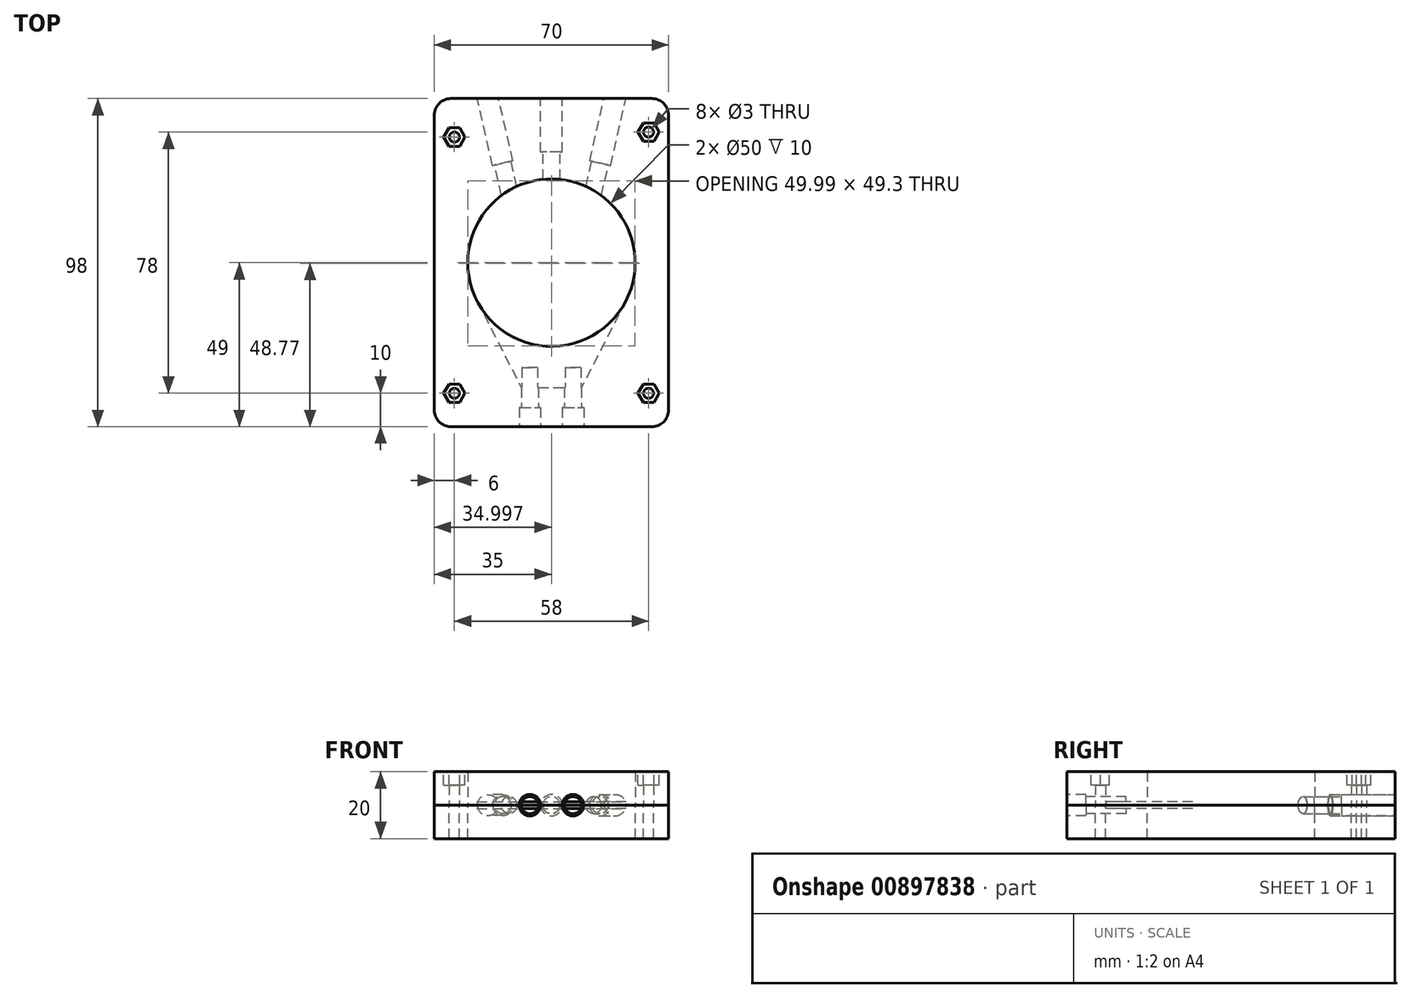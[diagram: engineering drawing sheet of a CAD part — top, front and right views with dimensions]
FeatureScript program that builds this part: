
annotation { "Feature Type Name" : "Feature", "Feature Type Description" : "" }
export const myFeature = defineFeature(function(context is Context, id is Id, definition is map)
    precondition{}
    {
        {
            var Q0;
            Q0=qCreatedBy(makeId("Front.planeOp"),FACE);
            var sketch = newSketch(context, id + "F0", { "sketchPlane" : qUnion([Q0])});
            skLineSegment(sketch, "E0.bottom", {"start": v(35, 5) * mm, "end": v(-35, 5) * mm});
            skLineSegment(sketch, "E0.top", {"start": v(35, -5) * mm, "end": v(-35, -5) * mm});
            skLineSegment(sketch, "E0.left", {"start": v(35, 5) * mm, "end": v(35, -5) * mm});
            skLineSegment(sketch, "E0.right", {"start": v(-35, 5) * mm, "end": v(-35, -5) * mm});
            skPoint(sketch, "E0.middle", {"position": v(0, 0) * mm});
            skSolve(sketch);
        }
        {
            var Q0;
            Q0 = qSketchRegion(id + "F0", true);
            extrude(context, id + "F1", {"entities" : qUnion([Q0]), "endBound" : BoundingType.SYMMETRIC, "depth" : 98 * mm, "offsetDistance" : 25 * mm});
        }
        {
            var Q0;
            Q0=makeQuery(id+"F1.opExtrude","SWEPT_FACE",FACE,{"disambiguationData":[OSD([sQuery(id+"F0.wireOp",EDGE,"E0.bottom")])]});
            var sketch = newSketch(context, id + "F2", { "sketchPlane" : qUnion([Q0])});
            skCircle(sketch, "E1", {"center": v(0, 0) * mm, "radius": 25 * mm});
            skSolve(sketch);
        }
        {
            var Q0;
            Q0 = qSketchRegion(id + "F2", true);
            extrude(context, id + "F3", {"entities" : qUnion([Q0]), "operationType" : NewBodyOperationType.REMOVE, "endBound" : BoundingType.THROUGH_ALL, "oppositeDirection" : true, "depth" : 25 * mm, "offsetDistance" : 25 * mm});
        }
        {
            var Q0;
            Q0=makeQuery(id+"F1.opExtrude","CAP_FACE",FACE,{"disambiguationData":[OSD([sQuery(id+"F0.wireOp",EDGE,"E0.bottom"),sQuery(id+"F0.wireOp",EDGE,"E0.top"),sQuery(id+"F0.wireOp",EDGE,"E0.left"),sQuery(id+"F0.wireOp",EDGE,"E0.right")])],"isStart":false});
            var sketch = newSketch(context, id + "F4", { "sketchPlane" : qUnion([Q0])});
            skCircle(sketch, "E2", {"center": v(-6.44, 5) * mm, "radius": 3.2 * mm});
            skCircle(sketch, "E3", {"center": v(6.44, 5) * mm, "radius": 3.2 * mm});
            skSolve(sketch);
        }
        {
            var Q0;
            Q0 = qSketchRegion(id + "F4", true);
            extrude(context, id + "F5", {"entities" : qUnion([Q0]), "operationType" : NewBodyOperationType.REMOVE, "oppositeDirection" : true, "depth" : 5.68 * mm, "offsetDistance" : 25 * mm});
        }
        {
            var Q0;
            Q0=makeQuery(id+"F5.boolean.opBoolean","COPY",FACE,{"derivedFrom":makeQuery(id+"F5.opExtrude","CAP_FACE",FACE,{"disambiguationData":[OSD([sQuery(id+"F4.wireOp",EDGE,"E2")])],"isStart":false})});
            var sketch = newSketch(context, id + "F6", { "sketchPlane" : qUnion([Q0])});
            skCircle(sketch, "E4", {"center": v(-6.44, 5) * mm, "radius": 2.55 * mm});
            skCircle(sketch, "E5", {"center": v(6.44, 5) * mm, "radius": 2.55 * mm});
            skSolve(sketch);
        }
        {
            var Q0;
            Q0 = qSketchRegion(id + "F6", true);
            extrude(context, id + "F7", {"entities" : qUnion([Q0]), "operationType" : NewBodyOperationType.REMOVE, "oppositeDirection" : true, "depth" : 12 * mm, "offsetDistance" : 25 * mm});
        }
        {
            var Q0;
            Q0=makeQuery(id+"F1.opExtrude","SWEPT_FACE",FACE,{"disambiguationData":[OSD([sQuery(id+"F0.wireOp",EDGE,"E0.bottom")])]});
            var sketch = newSketch(context, id + "F8", { "sketchPlane" : qUnion([Q0])});
            skLineSegment(sketch, "E6", {"start": v(-22.26, -11.39) * mm, "end": v(-9, -37.32) * mm});
            skLineSegment(sketch, "E7", {"start": v(0, 0) * mm, "end": v(0, -57.89) * mm, "construction": true});
            skLineSegment(sketch, "E8.MirrorCS", {"start": v(22.26, -11.39) * mm, "end": v(9, -37.32) * mm});
            skLineSegment(sketch, "E9", {"start": v(-9, -37.32) * mm, "end": v(9, -37.32) * mm});
            skLineSegment(sketch, "E10", {"start": v(22.26, -11.39) * mm, "end": v(-22.26, -11.39) * mm});
            skSolve(sketch);
        }
        {
            var Q0;
            Q0 = qSketchRegion(id + "F8", true);
            extrude(context, id + "F9", {"entities" : qUnion([Q0]), "operationType" : NewBodyOperationType.REMOVE, "oppositeDirection" : true, "depth" : 1 * mm, "offsetDistance" : 25 * mm});
        }
        {
            var Q0;
            Q0=makeQuery(id+"F1.opExtrude","CAP_FACE",FACE,{"disambiguationData":[OSD([sQuery(id+"F0.wireOp",EDGE,"E0.bottom"),sQuery(id+"F0.wireOp",EDGE,"E0.top"),sQuery(id+"F0.wireOp",EDGE,"E0.left"),sQuery(id+"F0.wireOp",EDGE,"E0.right")])],"isStart":true});
            var Q1;
            Q1=makeQuery(id+"F1.opExtrude","CAP_EDGE",EDGE,{"disambiguationData":[OSD([sQuery(id+"F0.wireOp",EDGE,"E0.right")])],"isStart":true});
            cPlane(context, id + "F10", {"entities" : qUnion([Q0, Q1]), "cplaneType" : CPlaneType.LINE_ANGLE, "offset" : 25 * mm, "angle" : 13 * degree, "oppositeDirection" : true, "width" : 150 * mm, "height" : 150 * mm});
        }
        {
            var Q0;
            Q0=makeQuery(id+"F1.opExtrude","CAP_FACE",FACE,{"disambiguationData":[OSD([sQuery(id+"F0.wireOp",EDGE,"E0.bottom"),sQuery(id+"F0.wireOp",EDGE,"E0.top"),sQuery(id+"F0.wireOp",EDGE,"E0.left"),sQuery(id+"F0.wireOp",EDGE,"E0.right")])],"isStart":true});
            var Q1;
            Q1=makeQuery(id+"F1.opExtrude","CAP_EDGE",EDGE,{"disambiguationData":[OSD([sQuery(id+"F0.wireOp",EDGE,"E0.left")])],"isStart":true});
            cPlane(context, id + "F11", {"entities" : qUnion([Q0, Q1]), "cplaneType" : CPlaneType.LINE_ANGLE, "offset" : 25 * mm, "angle" : 13 * degree, "width" : 150 * mm, "height" : 150 * mm});
        }
        {
            var Q0;
            Q0=qCreatedBy(id+"F10.planeOp",FACE);
            var sketch = newSketch(context, id + "F12", { "sketchPlane" : qUnion([Q0])});
            skCircle(sketch, "E11", {"center": v(-7.48, 5) * mm, "radius": 3.1 * mm});
            skSolve(sketch);
        }
        {
            var Q0;
            Q0 = qSketchRegion(id + "F12", true);
            extrude(context, id + "F13", {"entities" : qUnion([Q0]), "operationType" : NewBodyOperationType.REMOVE, "depth" : 15 * mm, "offsetDistance" : 25 * mm});
        }
        {
            var Q0;
            Q0=qCreatedBy(id+"F11.planeOp",FACE);
            var sketch = newSketch(context, id + "F14", { "sketchPlane" : qUnion([Q0])});
            skCircle(sketch, "E12", {"center": v(7.48, 5) * mm, "radius": 3.2 * mm});
            skSolve(sketch);
        }
        {
            var Q0;
            Q0 = qSketchRegion(id + "F14", true);
            extrude(context, id + "F15", {"entities" : qUnion([Q0]), "operationType" : NewBodyOperationType.REMOVE, "depth" : 23.4 * mm, "offsetDistance" : 25 * mm});
        }
        {
            var Q0;
            Q0 = qSketchRegion(id + "F12", true);
            extrude(context, id + "F16", {"entities" : qUnion([Q0]), "operationType" : NewBodyOperationType.REMOVE, "depth" : 23.4 * mm, "offsetDistance" : 25 * mm});
        }
        {
            var Q0;
            Q0=makeQuery(id+"F16.boolean.opBoolean","COPY",FACE,{"derivedFrom":makeQuery(id+"F16.opExtrude","CAP_FACE",FACE,{"disambiguationData":[OSD([sQuery(id+"F12.wireOp",EDGE,"E11")])],"isStart":false})});
            var sketch = newSketch(context, id + "F17", { "sketchPlane" : qUnion([Q0])});
            skCircle(sketch, "E13", {"center": v(7.48, 5) * mm, "radius": 2.55 * mm});
            skSolve(sketch);
        }
        {
            var Q0;
            Q0 = qSketchRegion(id + "F17", true);
            extrude(context, id + "F18", {"entities" : qUnion([Q0]), "operationType" : NewBodyOperationType.REMOVE, "oppositeDirection" : true, "depth" : 25 * mm, "offsetDistance" : 25 * mm});
        }
        {
            var Q0;
            Q0=makeQuery(id+"F15.boolean.opBoolean","COPY",FACE,{"derivedFrom":makeQuery(id+"F15.opExtrude","CAP_FACE",FACE,{"disambiguationData":[OSD([sQuery(id+"F14.wireOp",EDGE,"E12")])],"isStart":false})});
            var sketch = newSketch(context, id + "F19", { "sketchPlane" : qUnion([Q0])});
            skCircle(sketch, "E14", {"center": v(-7.48, 5) * mm, "radius": 2.55 * mm});
            skSolve(sketch);
        }
        {
            var Q0;
            Q0 = qSketchRegion(id + "F19", true);
            extrude(context, id + "F20", {"entities" : qUnion([Q0]), "operationType" : NewBodyOperationType.REMOVE, "oppositeDirection" : true, "depth" : 25 * mm, "offsetDistance" : 25 * mm});
        }
        {
            var Q0;
            Q0=makeQuery(id+"F1.opExtrude","CAP_FACE",FACE,{"disambiguationData":[OSD([sQuery(id+"F0.wireOp",EDGE,"E0.bottom"),sQuery(id+"F0.wireOp",EDGE,"E0.top"),sQuery(id+"F0.wireOp",EDGE,"E0.left"),sQuery(id+"F0.wireOp",EDGE,"E0.right")])],"isStart":true});
            var sketch = newSketch(context, id + "F21", { "sketchPlane" : qUnion([Q0])});
            skCircle(sketch, "E15", {"center": v(0, 5) * mm, "radius": 2.55 * mm});
            skSolve(sketch);
        }
        {
            var Q0;
            Q0 = qSketchRegion(id + "F21", true);
            extrude(context, id + "F22", {"entities" : qUnion([Q0]), "operationType" : NewBodyOperationType.REMOVE, "oppositeDirection" : true, "depth" : 25 * mm, "offsetDistance" : 25 * mm});
        }
        {
            var Q0;
            Q0=makeQuery(id+"F1.opExtrude","CAP_FACE",FACE,{"disambiguationData":[OSD([sQuery(id+"F0.wireOp",EDGE,"E0.bottom"),sQuery(id+"F0.wireOp",EDGE,"E0.top"),sQuery(id+"F0.wireOp",EDGE,"E0.left"),sQuery(id+"F0.wireOp",EDGE,"E0.right")])],"isStart":true});
            var sketch = newSketch(context, id + "F23", { "sketchPlane" : qUnion([Q0])});
            skCircle(sketch, "E16", {"center": v(0, 5) * mm, "radius": 3.2 * mm});
            skSolve(sketch);
        }
        {
            var Q0;
            Q0 = qSketchRegion(id + "F23", true);
            extrude(context, id + "F24", {"entities" : qUnion([Q0]), "operationType" : NewBodyOperationType.REMOVE, "oppositeDirection" : true, "depth" : 16 * mm, "offsetDistance" : 25 * mm});
        }
        {
            var Q0;
            {var subQ0=sQuery(id+"F0.wireOp",EDGE,"E0.bottom");var subQ1=makeQuery(id+"F1.opExtrude","SWEPT_FACE",FACE,{"disambiguationData":[OSD([subQ0])]});var subQ2=sQuery(id+"F8.wireOp",EDGE,"E6");var subQ3=makeQuery(id+"F9.opExtrude","SWEPT_FACE",FACE,{"disambiguationData":[OSD([subQ2])]});var subQ4=makeQuery(id+"F7.boolean.opBoolean","COPY",FACE,{"derivedFrom":makeQuery(id+"F7.opExtrude","SWEPT_FACE",FACE,{"disambiguationData":[OSD([sQuery(id+"F6.wireOp",EDGE,"E4")])]})});var subQ5=sQuery(id+"F8.wireOp",EDGE,"E9");var subQ6=sQuery(id+"F8.wireOp",EDGE,"E8.MirrorCS");var subQ7=makeQuery(id+"F9.opExtrude","SWEPT_FACE",FACE,{"disambiguationData":[OSD([subQ5])]});var subQ9=sQuery(id+"F4.wireOp",EDGE,"E2");var subQ10=makeQuery(id+"F5.boolean.opBoolean","COPY",FACE,{"derivedFrom":makeQuery(id+"F5.opExtrude","CAP_FACE",FACE,{"disambiguationData":[OSD([subQ9])],"isStart":false})});var subQ11=makeQuery(id+"F5.boolean.opBoolean","COPY",FACE,{"derivedFrom":makeQuery(id+"F5.opExtrude","SWEPT_FACE",FACE,{"disambiguationData":[OSD([subQ9])]})});var subQ12=sQuery(id+"F0.wireOp",EDGE,"E0.right");var subQ13=sQuery(id+"F0.wireOp",EDGE,"E0.left");var subQ14=sQuery(id+"F0.wireOp",EDGE,"E0.top");var subQ15=makeQuery(id+"F1.opExtrude","CAP_FACE",FACE,{"disambiguationData":[OSD([subQ0,subQ14,subQ13,subQ12])],"isStart":true});var subQ16=makeQuery(id+"F1.opExtrude","CAP_FACE",FACE,{"disambiguationData":[OSD([subQ0,subQ14,subQ13,subQ12])],"isStart":false});var subQ17=makeQuery(id+"F1.opExtrude","SWEPT_FACE",FACE,{"disambiguationData":[OSD([subQ12])]});var subQ18=makeQuery(id+"F3.boolean.opBoolean","COPY",FACE,{"derivedFrom":makeQuery(id+"F3.opExtrude","SWEPT_FACE",FACE,{"disambiguationData":[OSD([sQuery(id+"F2.wireOp",EDGE,"E1")])]})});var subQ19=sQuery(id+"F4.wireOp",EDGE,"E3");Q0=makeQuery(id+"F18.boolean.opBoolean","SPLIT",FACE,{"disambiguationData":[TD([subQ17])],"derivedFrom":makeQuery(id+"F9.boolean.opBoolean","SPLIT",FACE,{"disambiguationData":[TD([subQ15,subQ16,makeQuery(id+"F1.opExtrude","SWEPT_FACE",FACE,{"disambiguationData":[OSD([subQ13])]}),subQ17,subQ18,subQ11,subQ10,makeQuery(id+"F5.boolean.opBoolean","COPY",FACE,{"derivedFrom":makeQuery(id+"F5.opExtrude","SWEPT_FACE",FACE,{"disambiguationData":[OSD([subQ19])]})}),makeQuery(id+"F5.boolean.opBoolean","COPY",FACE,{"derivedFrom":makeQuery(id+"F5.opExtrude","CAP_FACE",FACE,{"disambiguationData":[OSD([subQ19])],"isStart":false})}),subQ4,makeQuery(id+"F7.boolean.opBoolean","COPY",FACE,{"derivedFrom":makeQuery(id+"F7.opExtrude","SWEPT_FACE",FACE,{"disambiguationData":[OSD([sQuery(id+"F6.wireOp",EDGE,"E5")])]})}),subQ3,makeQuery(id+"F9.opExtrude","SWEPT_FACE",FACE,{"disambiguationData":[OSD([subQ6])]}),subQ7])],"derivedFrom":subQ1})});}
            var sketch = newSketch(context, id + "F25", { "sketchPlane" : qUnion([Q0])});
            skCircle(sketch, "E17", {"center": v(-29, 37.5) * mm, "radius": 1.5 * mm});
            skCircle(sketch, "E18", {"center": v(29, 39) * mm, "radius": 1.5 * mm});
            skCircle(sketch, "E19", {"center": v(-29, -39) * mm, "radius": 1.5 * mm});
            skCircle(sketch, "E20", {"center": v(29, -39) * mm, "radius": 1.5 * mm});
            skSolve(sketch);
        }
        {
            var Q0;
            Q0 = qSketchRegion(id + "F25", true);
            extrude(context, id + "F26", {"entities" : qUnion([Q0]), "operationType" : NewBodyOperationType.REMOVE, "oppositeDirection" : true, "depth" : 25 * mm, "offsetDistance" : 25 * mm});
        }
        {
            var Q0;
            Q0=makeQuery(id+"F1.opExtrude","SWEPT_BODY",BODY,{"disambiguationData":[OSD([sQuery(id+"F0.wireOp",EDGE,"E0.bottom"),sQuery(id+"F0.wireOp",EDGE,"E0.top"),sQuery(id+"F0.wireOp",EDGE,"E0.left"),sQuery(id+"F0.wireOp",EDGE,"E0.right")])]});
            var Q1;
            {var subQ0=sQuery(id+"F0.wireOp",EDGE,"E0.bottom");var subQ1=makeQuery(id+"F1.opExtrude","SWEPT_FACE",FACE,{"disambiguationData":[OSD([subQ0])]});var subQ2=sQuery(id+"F8.wireOp",EDGE,"E6");var subQ3=makeQuery(id+"F9.opExtrude","SWEPT_FACE",FACE,{"disambiguationData":[OSD([subQ2])]});var subQ4=makeQuery(id+"F7.boolean.opBoolean","COPY",FACE,{"derivedFrom":makeQuery(id+"F7.opExtrude","SWEPT_FACE",FACE,{"disambiguationData":[OSD([sQuery(id+"F6.wireOp",EDGE,"E4")])]})});var subQ5=sQuery(id+"F8.wireOp",EDGE,"E9");var subQ6=sQuery(id+"F8.wireOp",EDGE,"E8.MirrorCS");var subQ7=makeQuery(id+"F9.opExtrude","SWEPT_FACE",FACE,{"disambiguationData":[OSD([subQ5])]});var subQ9=sQuery(id+"F4.wireOp",EDGE,"E2");var subQ10=makeQuery(id+"F5.boolean.opBoolean","COPY",FACE,{"derivedFrom":makeQuery(id+"F5.opExtrude","CAP_FACE",FACE,{"disambiguationData":[OSD([subQ9])],"isStart":false})});var subQ11=makeQuery(id+"F5.boolean.opBoolean","COPY",FACE,{"derivedFrom":makeQuery(id+"F5.opExtrude","SWEPT_FACE",FACE,{"disambiguationData":[OSD([subQ9])]})});var subQ12=sQuery(id+"F0.wireOp",EDGE,"E0.right");var subQ13=sQuery(id+"F0.wireOp",EDGE,"E0.left");var subQ14=sQuery(id+"F0.wireOp",EDGE,"E0.top");var subQ15=makeQuery(id+"F1.opExtrude","CAP_FACE",FACE,{"disambiguationData":[OSD([subQ0,subQ14,subQ13,subQ12])],"isStart":true});var subQ16=makeQuery(id+"F1.opExtrude","CAP_FACE",FACE,{"disambiguationData":[OSD([subQ0,subQ14,subQ13,subQ12])],"isStart":false});var subQ17=makeQuery(id+"F1.opExtrude","SWEPT_FACE",FACE,{"disambiguationData":[OSD([subQ12])]});var subQ18=makeQuery(id+"F3.boolean.opBoolean","COPY",FACE,{"derivedFrom":makeQuery(id+"F3.opExtrude","SWEPT_FACE",FACE,{"disambiguationData":[OSD([sQuery(id+"F2.wireOp",EDGE,"E1")])]})});var subQ19=sQuery(id+"F4.wireOp",EDGE,"E3");Q1=makeQuery(id+"F18.boolean.opBoolean","SPLIT",FACE,{"disambiguationData":[TD([subQ17])],"derivedFrom":makeQuery(id+"F9.boolean.opBoolean","SPLIT",FACE,{"disambiguationData":[TD([subQ15,subQ16,makeQuery(id+"F1.opExtrude","SWEPT_FACE",FACE,{"disambiguationData":[OSD([subQ13])]}),subQ17,subQ18,subQ11,subQ10,makeQuery(id+"F5.boolean.opBoolean","COPY",FACE,{"derivedFrom":makeQuery(id+"F5.opExtrude","SWEPT_FACE",FACE,{"disambiguationData":[OSD([subQ19])]})}),makeQuery(id+"F5.boolean.opBoolean","COPY",FACE,{"derivedFrom":makeQuery(id+"F5.opExtrude","CAP_FACE",FACE,{"disambiguationData":[OSD([subQ19])],"isStart":false})}),subQ4,makeQuery(id+"F7.boolean.opBoolean","COPY",FACE,{"derivedFrom":makeQuery(id+"F7.opExtrude","SWEPT_FACE",FACE,{"disambiguationData":[OSD([sQuery(id+"F6.wireOp",EDGE,"E5")])]})}),subQ3,makeQuery(id+"F9.opExtrude","SWEPT_FACE",FACE,{"disambiguationData":[OSD([subQ6])]}),subQ7])],"derivedFrom":subQ1})});}
            mirror(context, id + "F27", {"entities" : qUnion([Q0]), "mirrorPlane" : qUnion([Q1])});
        }
        {
            var Q0;
            Q0=makeQuery(id+"F27.opPattern","COPY",FACE,{"derivedFrom":makeQuery(id+"F1.opExtrude","SWEPT_FACE",FACE,{"disambiguationData":[OSD([sQuery(id+"F0.wireOp",EDGE,"E0.top")])]}),"instanceName":"1"});
            var sketch = newSketch(context, id + "F28", { "sketchPlane" : qUnion([Q0])});
            skCircle(sketch, "E21.cCircle", {"center": v(-29, 37.5) * mm, "radius": 2.75 * mm, "construction": true});
            skLineSegment(sketch, "E21.0", {"start": v(-25.82, 37.5) * mm, "end": v(-27.41, 34.75) * mm});
            skLineSegment(sketch, "E21.1", {"start": v(-27.41, 34.75) * mm, "end": v(-30.59, 34.75) * mm});
            skLineSegment(sketch, "E21.2", {"start": v(-30.59, 34.75) * mm, "end": v(-32.18, 37.5) * mm});
            skLineSegment(sketch, "E21.3", {"start": v(-32.18, 37.5) * mm, "end": v(-30.59, 40.25) * mm});
            skLineSegment(sketch, "E21.4", {"start": v(-30.59, 40.25) * mm, "end": v(-27.41, 40.25) * mm});
            skLineSegment(sketch, "E21.5", {"start": v(-27.41, 40.25) * mm, "end": v(-25.82, 37.5) * mm});
            skPoint(sketch, "E21.0.midPoint", {"position": v(-26.62, 36.13) * mm});
            skCircle(sketch, "E22.cCircle", {"center": v(29, 39) * mm, "radius": 2.75 * mm, "construction": true});
            skLineSegment(sketch, "E22.0", {"start": v(32.18, 39) * mm, "end": v(30.59, 36.25) * mm});
            skLineSegment(sketch, "E22.1", {"start": v(30.59, 36.25) * mm, "end": v(27.41, 36.25) * mm});
            skLineSegment(sketch, "E22.2", {"start": v(27.41, 36.25) * mm, "end": v(25.82, 39) * mm});
            skLineSegment(sketch, "E22.3", {"start": v(25.82, 39) * mm, "end": v(27.41, 41.75) * mm});
            skLineSegment(sketch, "E22.4", {"start": v(27.41, 41.75) * mm, "end": v(30.59, 41.75) * mm});
            skLineSegment(sketch, "E22.5", {"start": v(30.59, 41.75) * mm, "end": v(32.18, 39) * mm});
            skPoint(sketch, "E22.0.midPoint", {"position": v(31.38, 37.62) * mm});
            skCircle(sketch, "E23.cCircle", {"center": v(-29, -39) * mm, "radius": 2.75 * mm, "construction": true});
            skLineSegment(sketch, "E23.0", {"start": v(-25.82, -39) * mm, "end": v(-27.41, -41.75) * mm});
            skLineSegment(sketch, "E23.1", {"start": v(-27.41, -41.75) * mm, "end": v(-30.59, -41.75) * mm});
            skLineSegment(sketch, "E23.2", {"start": v(-30.59, -41.75) * mm, "end": v(-32.18, -39) * mm});
            skLineSegment(sketch, "E23.3", {"start": v(-32.18, -39) * mm, "end": v(-30.59, -36.25) * mm});
            skLineSegment(sketch, "E23.4", {"start": v(-30.59, -36.25) * mm, "end": v(-27.41, -36.25) * mm});
            skLineSegment(sketch, "E23.5", {"start": v(-27.41, -36.25) * mm, "end": v(-25.82, -39) * mm});
            skPoint(sketch, "E23.0.midPoint", {"position": v(-26.62, -40.38) * mm});
            skCircle(sketch, "E24.cCircle", {"center": v(29, -39) * mm, "radius": 2.75 * mm, "construction": true});
            skLineSegment(sketch, "E24.0", {"start": v(30.59, -41.75) * mm, "end": v(27.41, -41.75) * mm});
            skLineSegment(sketch, "E24.1", {"start": v(27.41, -41.75) * mm, "end": v(25.82, -39) * mm});
            skLineSegment(sketch, "E24.2", {"start": v(25.82, -39) * mm, "end": v(27.41, -36.25) * mm});
            skLineSegment(sketch, "E24.3", {"start": v(27.41, -36.25) * mm, "end": v(30.59, -36.25) * mm});
            skLineSegment(sketch, "E24.4", {"start": v(30.59, -36.25) * mm, "end": v(32.18, -39) * mm});
            skLineSegment(sketch, "E24.5", {"start": v(32.18, -39) * mm, "end": v(30.59, -41.75) * mm});
            skPoint(sketch, "E24.0.midPoint", {"position": v(29, -41.75) * mm});
            skSolve(sketch);
        }
        {
            var Q0;
            Q0 = qSketchRegion(id + "F28", true);
            extrude(context, id + "F29", {"entities" : qUnion([Q0]), "operationType" : NewBodyOperationType.REMOVE, "oppositeDirection" : true, "depth" : 4 * mm, "offsetDistance" : 25 * mm});
        }
        {
            var Q0;
            Q0=makeQuery(id+"F27.opPattern","COPY",EDGE,{"derivedFrom":makeQuery(id+"F1.opExtrude","CAP_EDGE",EDGE,{"disambiguationData":[OSD([sQuery(id+"F0.wireOp",EDGE,"E0.right")])],"isStart":false}),"instanceName":"1"});
            var Q1;
            Q1=makeQuery(id+"F1.opExtrude","CAP_EDGE",EDGE,{"disambiguationData":[OSD([sQuery(id+"F0.wireOp",EDGE,"E0.right")])],"isStart":false});
            var Q2;
            Q2=makeQuery(id+"F27.opPattern","COPY",EDGE,{"derivedFrom":makeQuery(id+"F1.opExtrude","CAP_EDGE",EDGE,{"disambiguationData":[OSD([sQuery(id+"F0.wireOp",EDGE,"E0.left")])],"isStart":false}),"instanceName":"1"});
            var Q3;
            Q3=makeQuery(id+"F1.opExtrude","CAP_EDGE",EDGE,{"disambiguationData":[OSD([sQuery(id+"F0.wireOp",EDGE,"E0.left")])],"isStart":false});
            var Q4;
            Q4=makeQuery(id+"F27.opPattern","COPY",EDGE,{"derivedFrom":makeQuery(id+"F1.opExtrude","CAP_EDGE",EDGE,{"disambiguationData":[OSD([sQuery(id+"F0.wireOp",EDGE,"E0.left")])],"isStart":true}),"instanceName":"1"});
            var Q5;
            Q5=makeQuery(id+"F1.opExtrude","CAP_EDGE",EDGE,{"disambiguationData":[OSD([sQuery(id+"F0.wireOp",EDGE,"E0.left")])],"isStart":true});
            var Q6;
            Q6=makeQuery(id+"F27.opPattern","COPY",EDGE,{"derivedFrom":makeQuery(id+"F1.opExtrude","CAP_EDGE",EDGE,{"disambiguationData":[OSD([sQuery(id+"F0.wireOp",EDGE,"E0.right")])],"isStart":true}),"instanceName":"1"});
            var Q7;
            Q7=makeQuery(id+"F1.opExtrude","CAP_EDGE",EDGE,{"disambiguationData":[OSD([sQuery(id+"F0.wireOp",EDGE,"E0.right")])],"isStart":true});
            fillet(context, id + "F30", {"entities" : qUnion([Q0, Q1, Q2, Q3, Q4, Q5, Q6, Q7]), "radius" : 5 * mm, "tangentPropagation" : true, "allowEdgeOverflow" : false});
        }
    });
